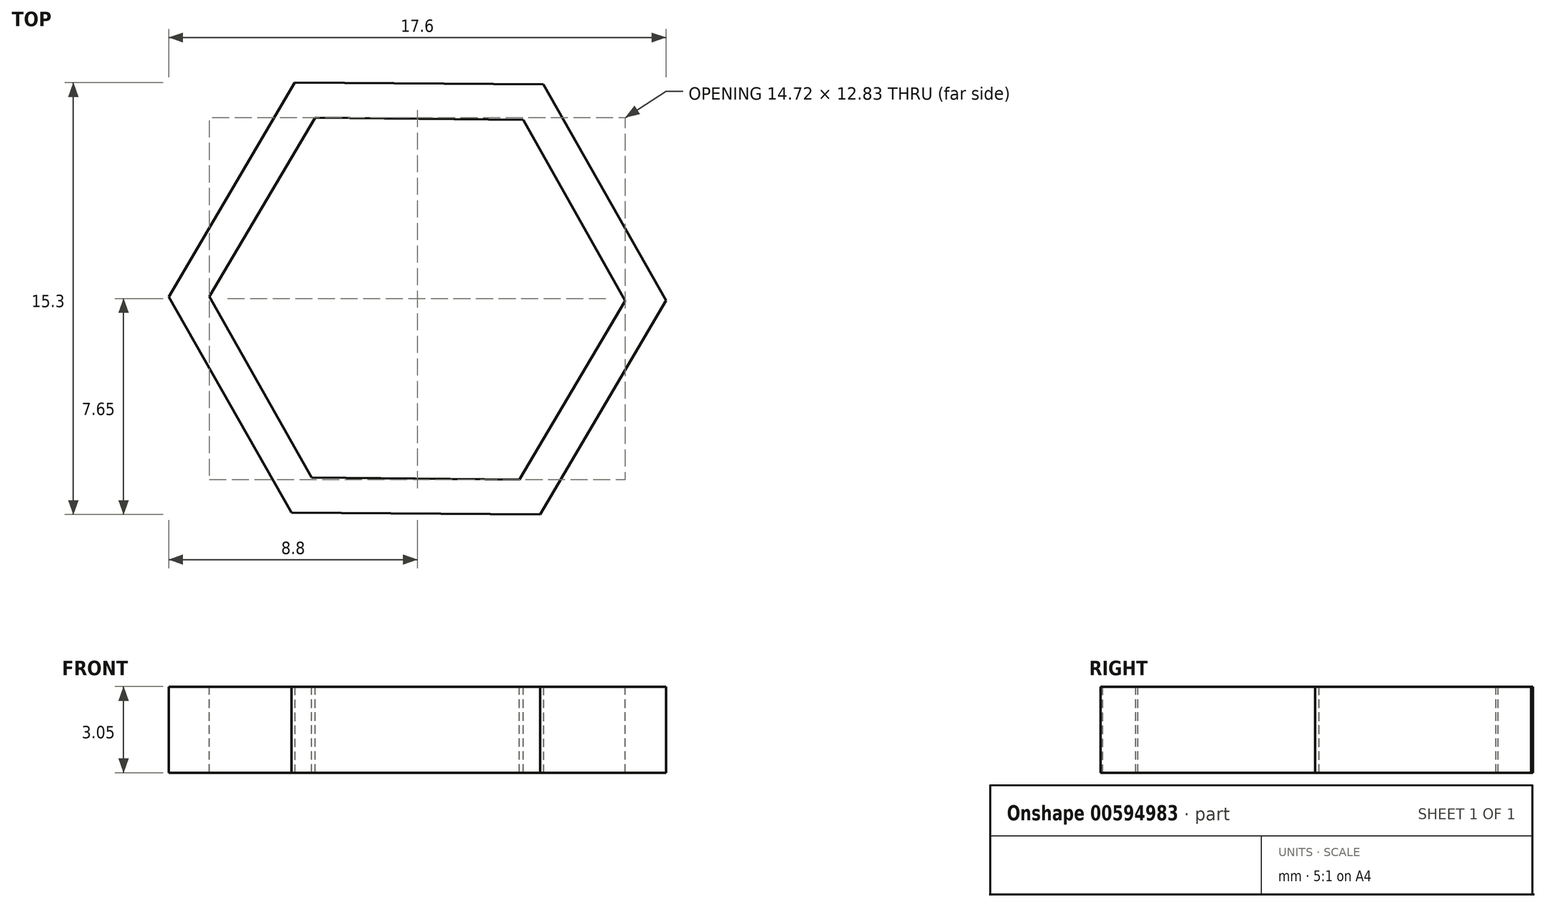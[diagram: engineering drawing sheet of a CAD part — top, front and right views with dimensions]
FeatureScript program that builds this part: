
annotation { "Feature Type Name" : "Feature", "Feature Type Description" : "" }
export const myFeature = defineFeature(function(context is Context, id is Id, definition is map)
    precondition{}
    {
        {
            var Q0;
            Q0=qCreatedBy(makeId("Top.planeOp"),FACE);
            var sketch = newSketch(context, id + "F0", { "sketchPlane" : qUnion([Q0])});
            skCircle(sketch, "E0.cCircle", {"center": v(0, 0) * mm, "radius": 7.62 * mm, "construction": true});
            skLineSegment(sketch, "E0.0", {"start": v(8.8, -0.06) * mm, "end": v(4.34, -7.65) * mm});
            skLineSegment(sketch, "E0.1", {"start": v(4.34, -7.65) * mm, "end": v(-4.45, -7.59) * mm});
            skLineSegment(sketch, "E0.2", {"start": v(-4.45, -7.59) * mm, "end": v(-8.8, 0.06) * mm});
            skLineSegment(sketch, "E0.3", {"start": v(-8.8, 0.06) * mm, "end": v(-4.34, 7.65) * mm});
            skLineSegment(sketch, "E0.4", {"start": v(-4.34, 7.65) * mm, "end": v(4.45, 7.59) * mm});
            skLineSegment(sketch, "E0.5", {"start": v(4.45, 7.59) * mm, "end": v(8.8, -0.06) * mm});
            skPoint(sketch, "E0.0.midPoint", {"position": v(6.57, -3.86) * mm});
            skSolve(sketch);
        }
        {
            var Q0;
            Q0 = qSketchRegion(id + "F0", true);
            extrude(context, id + "F1", {"entities" : qUnion([Q0]), "depth" : 3.05 * mm, "offsetDistance" : 25.4 * mm});
        }
        {
            var Q0;
            Q0=makeQuery(id+"F1.opExtrude","CAP_FACE",FACE,{"disambiguationData":[OSD([sQuery(id+"F0.wireOp",EDGE,"E0.0"),sQuery(id+"F0.wireOp",EDGE,"E0.1"),sQuery(id+"F0.wireOp",EDGE,"E0.2"),sQuery(id+"F0.wireOp",EDGE,"E0.3"),sQuery(id+"F0.wireOp",EDGE,"E0.4"),sQuery(id+"F0.wireOp",EDGE,"E0.5")])],"isStart":false});
            var sketch = newSketch(context, id + "F2", { "sketchPlane" : qUnion([Q0])});
            skCircle(sketch, "E1.cCircle", {"center": v(0, 0) * mm, "radius": 6.38 * mm, "construction": true});
            skLineSegment(sketch, "E1.0", {"start": v(3.75, 6.34) * mm, "end": v(7.36, -0.08) * mm});
            skLineSegment(sketch, "E1.1", {"start": v(7.36, -0.08) * mm, "end": v(3.61, -6.41) * mm});
            skLineSegment(sketch, "E1.2", {"start": v(3.61, -6.41) * mm, "end": v(-3.75, -6.34) * mm});
            skLineSegment(sketch, "E1.3", {"start": v(-3.75, -6.34) * mm, "end": v(-7.36, 0.08) * mm});
            skLineSegment(sketch, "E1.4", {"start": v(-7.36, 0.08) * mm, "end": v(-3.61, 6.41) * mm});
            skLineSegment(sketch, "E1.5", {"start": v(-3.61, 6.41) * mm, "end": v(3.75, 6.34) * mm});
            skPoint(sketch, "E1.0.midPoint", {"position": v(5.55, 3.13) * mm});
            skSolve(sketch);
        }
        {
            var Q0;
            Q0=makeQuery(id+"F2.imprint","IMPRINT",FACE,{"disambiguationData":[TD([[makeQuery(id+"F2.imprint","IMPRINT",EDGE,{"derivedFrom":sQuery(id+"F2.wireOp",EDGE,"E1.0")}),-1.0]])]});
            extrude(context, id + "F3", {"entities" : qUnion([Q0]), "operationType" : NewBodyOperationType.REMOVE, "oppositeDirection" : true, "depth" : 88.65 * mm, "offsetDistance" : 25.4 * mm});
        }
    });
